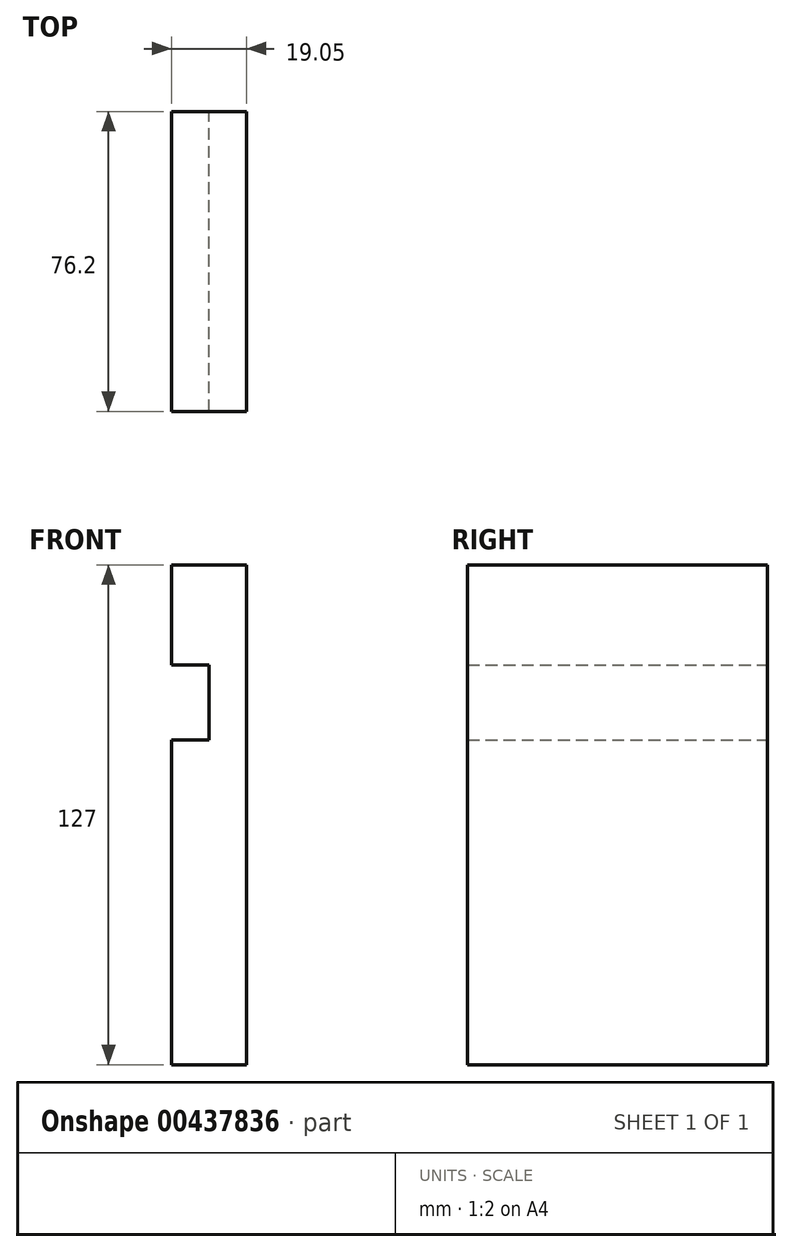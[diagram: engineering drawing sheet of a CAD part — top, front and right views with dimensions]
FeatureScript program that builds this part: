
annotation { "Feature Type Name" : "Feature", "Feature Type Description" : "" }
export const myFeature = defineFeature(function(context is Context, id is Id, definition is map)
    precondition{}
    {
        {
            var Q0;
            Q0=qCreatedBy(makeId("Front.planeOp"),FACE);
            var sketch = newSketch(context, id + "F0", { "sketchPlane" : qUnion([Q0])});
            skLineSegment(sketch, "E0", {"start": v(29.17, 73.8) * mm, "end": v(29.17, -53.2) * mm});
            skLineSegment(sketch, "E1", {"start": v(29.17, -53.2) * mm, "end": v(10.12, -53.2) * mm});
            skLineSegment(sketch, "E2", {"start": v(29.17, 73.8) * mm, "end": v(10.12, 73.8) * mm});
            skLineSegment(sketch, "E3", {"start": v(10.12, 73.8) * mm, "end": v(10.12, 48.4) * mm});
            skLineSegment(sketch, "E4", {"start": v(10.12, 48.4) * mm, "end": v(19.64, 48.4) * mm});
            skLineSegment(sketch, "E5", {"start": v(19.64, 48.4) * mm, "end": v(19.64, 29.36) * mm});
            skLineSegment(sketch, "E6", {"start": v(19.64, 29.36) * mm, "end": v(10.12, 29.36) * mm});
            skLineSegment(sketch, "E7", {"start": v(10.12, 29.36) * mm, "end": v(10.12, -53.2) * mm});
            skSolve(sketch);
        }
        {
            var Q0;
            Q0=makeQuery(id+"F0.imprint","IMPRINT",FACE,{"disambiguationData":[TD([[makeQuery(id+"F0.imprint","IMPRINT",EDGE,{"derivedFrom":sQuery(id+"F0.wireOp",EDGE,"E0")}),-1.0]])]});
            extrude(context, id + "F1", {"entities" : qUnion([Q0]), "depth" : 76.2 * mm});
        }
    });
